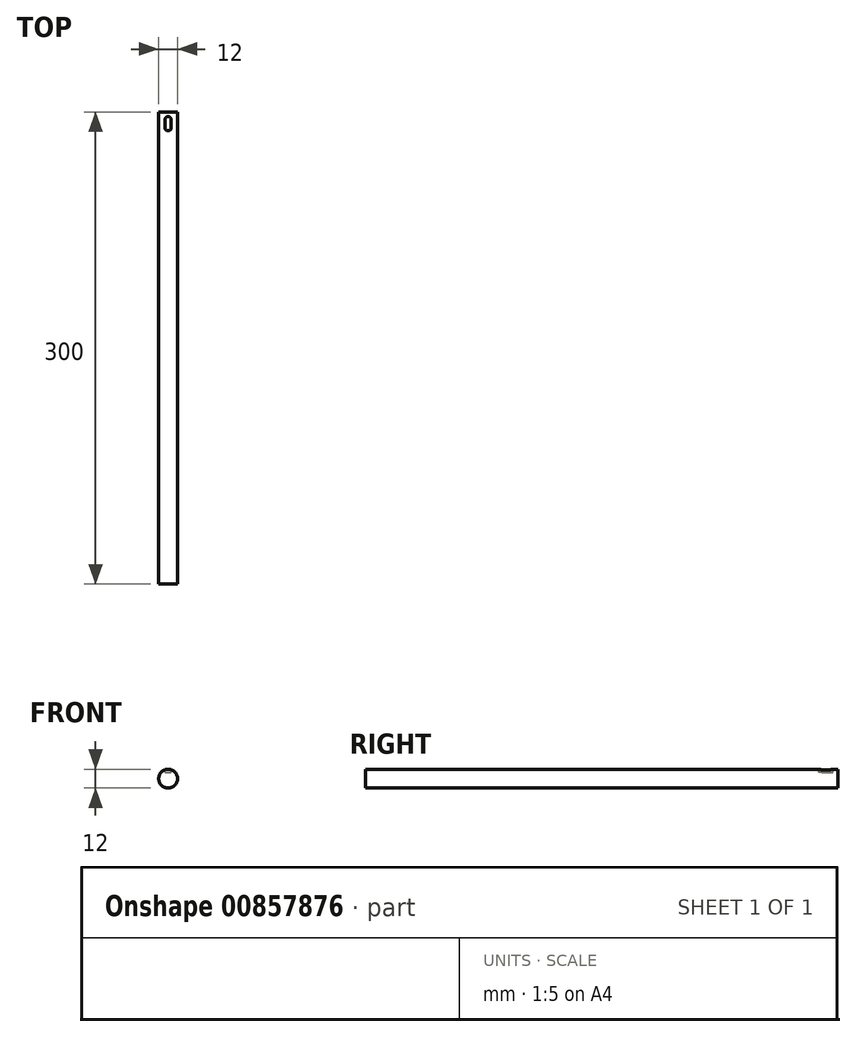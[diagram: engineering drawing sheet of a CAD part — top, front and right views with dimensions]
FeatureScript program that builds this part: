
annotation { "Feature Type Name" : "Feature", "Feature Type Description" : "" }
export const myFeature = defineFeature(function(context is Context, id is Id, definition is map)
    precondition{}
    {
        {
            var Q0;
            Q0=qCreatedBy(makeId("Front.planeOp"),FACE);
            var sketch = newSketch(context, id + "F0", { "sketchPlane" : qUnion([Q0])});
            skCircle(sketch, "E0", {"center": v(0, 0) * mm, "radius": 6 * mm});
            skSolve(sketch);
        }
        {
            var Q0;
            Q0=makeQuery(id+"F0.imprint","IMPRINT",FACE,{"disambiguationData":[TD([[makeQuery(id+"F0.imprint","IMPRINT",EDGE,{"derivedFrom":sQuery(id+"F0.wireOp",EDGE,"E0")}),1.0]])]});
            extrude(context, id + "F1", {"entities" : qUnion([Q0]), "depth" : 300 * mm, "offsetDistance" : 25 * mm});
        }
        {
            var Q0;
            Q0=qCreatedBy(makeId("Top.planeOp"),FACE);
            cPlane(context, id + "F2", {"entities" : qUnion([Q0]), "cplaneType" : CPlaneType.OFFSET, "offset" : 8 * mm, "width" : 150 * mm, "height" : 150 * mm});
        }
        {
            var Q0;
            Q0=qCreatedBy(id+"F2.planeOp",FACE);
            var sketch = newSketch(context, id + "F3", { "sketchPlane" : qUnion([Q0])});
            skArc(sketch, "E1", {"start": v(-2, -10) * mm, "mid": v(0, -12) * mm, "end": v(2, -10) * mm});
            skLineSegment(sketch, "E2", {"start": v(-11.07, -10) * mm, "end": v(10.62, -10) * mm, "construction": true});
            skLineSegment(sketch, "E3", {"start": v(-11.07, -5) * mm, "end": v(11.3, -5) * mm, "construction": true});
            skLineSegment(sketch, "E4", {"start": v(2, -10) * mm, "end": v(2, -5) * mm});
            skLineSegment(sketch, "E5", {"start": v(-2, -10) * mm, "end": v(-2, -5) * mm});
            skArc(sketch, "E6", {"start": v(2, -5) * mm, "mid": v(0, -3) * mm, "end": v(-2, -5) * mm});
            skSolve(sketch);
        }
        {
            var Q0;
            Q0=makeQuery(id+"F3.imprint","IMPRINT",FACE,{"disambiguationData":[TD([[makeQuery(id+"F3.imprint","IMPRINT",EDGE,{"derivedFrom":sQuery(id+"F3.wireOp",EDGE,"E1")}),1.0]])]});
            extrude(context, id + "F4", {"entities" : qUnion([Q0]), "operationType" : NewBodyOperationType.REMOVE, "oppositeDirection" : true, "depth" : 4 * mm, "offsetDistance" : 25 * mm});
        }
    });
